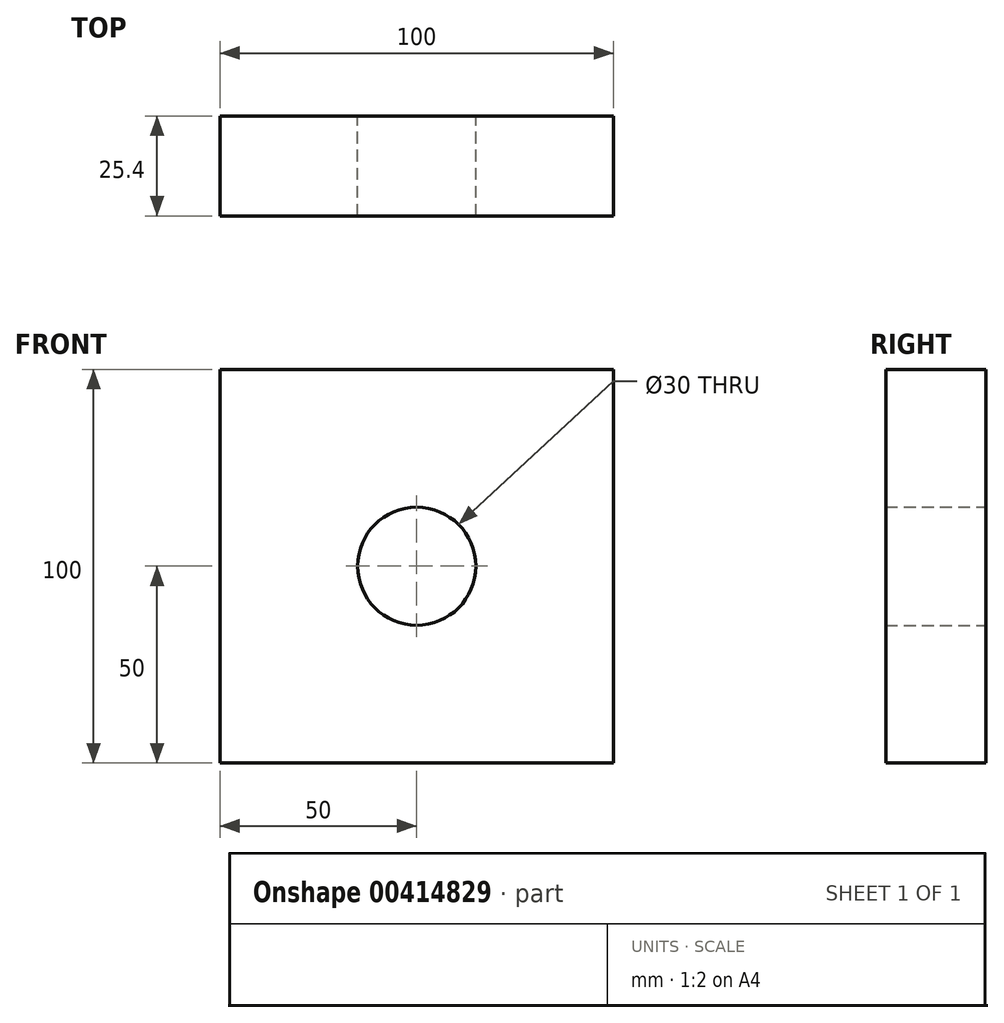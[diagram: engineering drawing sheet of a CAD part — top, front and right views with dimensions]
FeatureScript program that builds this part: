
annotation { "Feature Type Name" : "Feature", "Feature Type Description" : "" }
export const myFeature = defineFeature(function(context is Context, id is Id, definition is map)
    precondition{}
    {
        {
            var Q0;
            Q0=qCreatedBy(makeId("Front.planeOp"),FACE);
            var sketch = newSketch(context, id + "F0", { "sketchPlane" : qUnion([Q0])});
            skCircle(sketch, "E0", {"center": v(0, 0) * mm, "radius": 15 * mm});
            skLineSegment(sketch, "E1", {"start": v(-50, 50) * mm, "end": v(50, 50) * mm});
            skLineSegment(sketch, "E2", {"start": v(-50, 50) * mm, "end": v(-50, -50) * mm});
            skLineSegment(sketch, "E3", {"start": v(-50, -50) * mm, "end": v(50, -50) * mm});
            skLineSegment(sketch, "E4", {"start": v(50, 50) * mm, "end": v(50, -50) * mm});
            skSolve(sketch);
        }
        {
            var Q0;
            Q0=makeQuery(id+"F0.imprint","IMPRINT",FACE,{"disambiguationData":[TD([[makeQuery(id+"F0.imprint","IMPRINT",EDGE,{"derivedFrom":sQuery(id+"F0.wireOp",EDGE,"E0")}),-1.0]])]});
            extrude(context, id + "F1", {"entities" : qUnion([Q0]), "depth" : 25.4 * mm});
        }
    });
